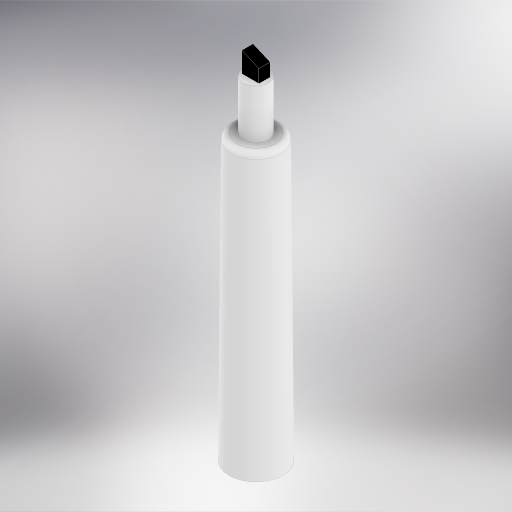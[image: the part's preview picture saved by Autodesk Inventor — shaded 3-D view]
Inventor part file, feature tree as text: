
AUTODESK INVENTOR PART (.ipt)
format: ipt  version: 2023 (Build 270158000, 158)  size: 428,544 bytes
history: native  units: mm
features: sketch x6, extrude x4, other x1, plane x1, loft x1, fillet x1
ambient origin geometry x8: Origin, YZ Plane, XZ Plane, XY Plane, X Axis, Y Axis, Z Axis, Center Point
bodies: Body1 (feature_tree)
feature tree (14):
  other  "Sólido1"
  sketch  "Boceto1"  dims[d0=18.5mm d1=97.4mm]
  plane  "Plano de trabajo1"
  loft  "Solevación1"
  extrude  "Extrusión1"  TaperAngle=0.0deg  [1 undecoded]
  fillet  "Empalme1"  [1 undecoded]
  extrude  "Extrusión2"  Depth=17.1mm TaperAngle=0.0deg
  extrude  "Extrusión3"  Depth=5.9mm
  extrude  "Extrusión4"  Depth=3.84mm TaperAngle=0.0deg
  sketch  "Boceto2"  dims[d2=17.0mm d3=0.0mm d4=90.0deg d5=0.0mm d6=90.0deg]
  sketch  "Boceto3"  dims[d7=8.7mm d8=17.1mm d9=0.0mm]
  sketch  "Boceto4"  dims[d10=2.0mm d11=5.9mm]
  sketch  "Boceto5"  dims[d12=3.84mm d13=4.5mm d14=0.0mm]
  sketch  "Boceto6"  dims[d15=2.5mm d16=4.5mm d17=0.0mm d18=14.0mm d19=2.7mm d20=0.65mm d21=90.0deg d22=0.65mm d23=180.0deg d24=90.0deg d25=80.0mm d27=360.0deg d29=10.0mm d30=0.0mm]
note: 2 required parameter values undecoded (feature->parameter linkage not recoverable at this tier; creation-order binding heuristic only, values carry confidence <= 0.55)
